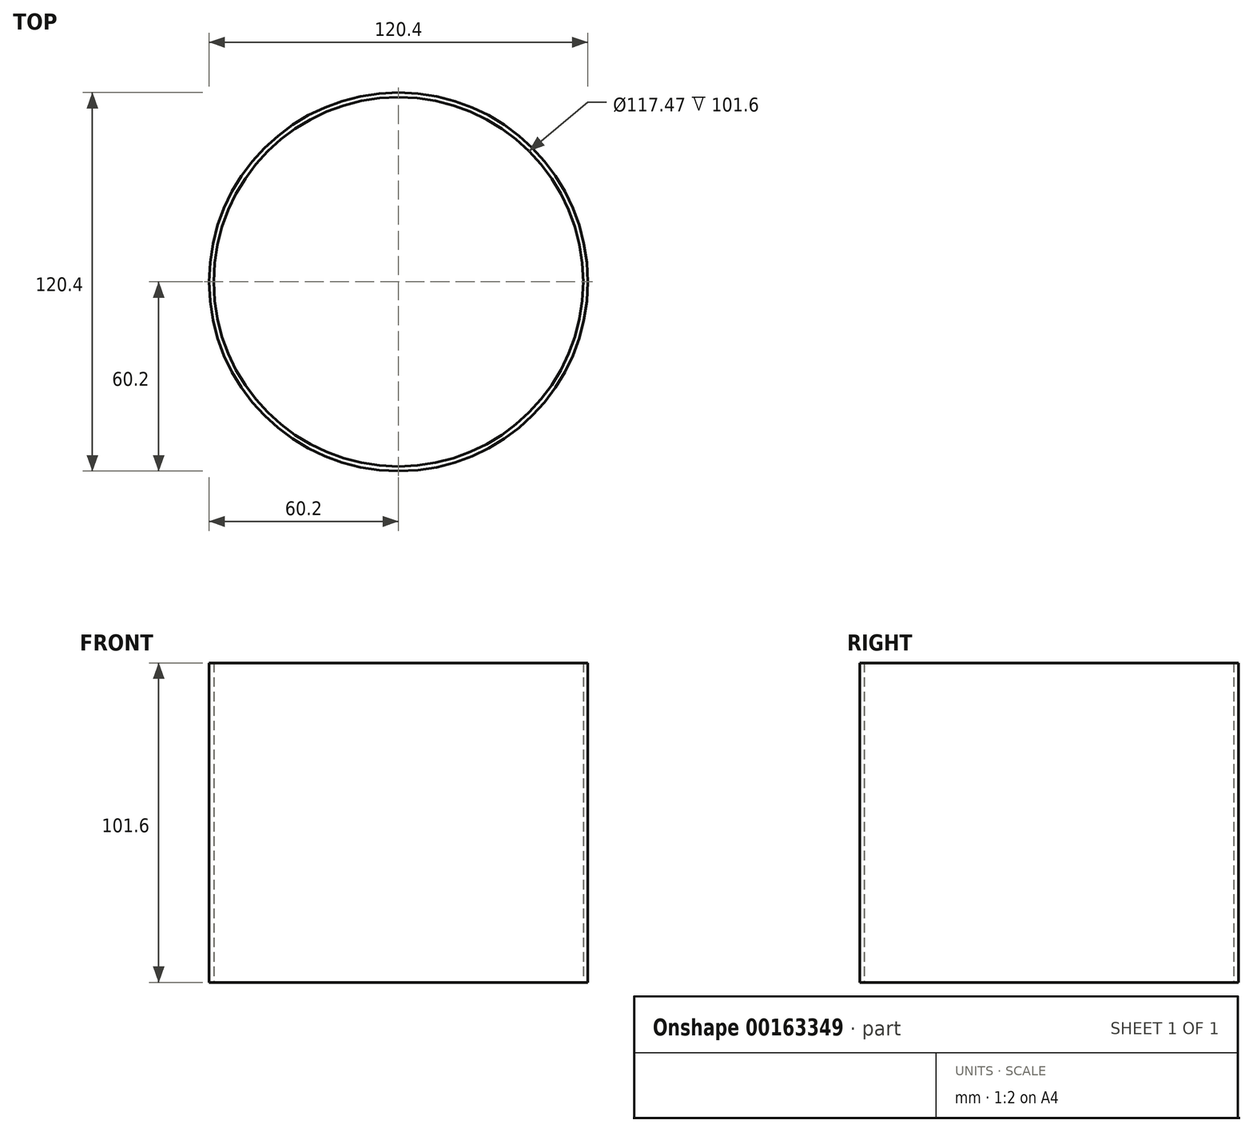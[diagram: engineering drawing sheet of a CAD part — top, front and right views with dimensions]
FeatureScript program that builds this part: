
annotation { "Feature Type Name" : "Feature", "Feature Type Description" : "" }
export const myFeature = defineFeature(function(context is Context, id is Id, definition is map)
    precondition{}
    {
        {
            var Q0;
            Q0=qCreatedBy(makeId("Top.planeOp"),FACE);
            var sketch = newSketch(context, id + "F0", { "sketchPlane" : qUnion([Q0])});
            skCircle(sketch, "E0", {"center": v(0, 0) * mm, "radius": 60.2 * mm});
            skCircle(sketch, "E1", {"center": v(0, 0) * mm, "radius": 58.74 * mm});
            skSolve(sketch);
        }
        {
            var Q0;
            Q0=makeQuery(id+"F0.imprint","IMPRINT",FACE,{"disambiguationData":[TD([[makeQuery(id+"F0.imprint","IMPRINT",EDGE,{"derivedFrom":sQuery(id+"F0.wireOp",EDGE,"E0")}),1.0]])]});
            extrude(context, id + "F1", {"entities" : qUnion([Q0]), "depth" : 101.6 * mm});
        }
    });
